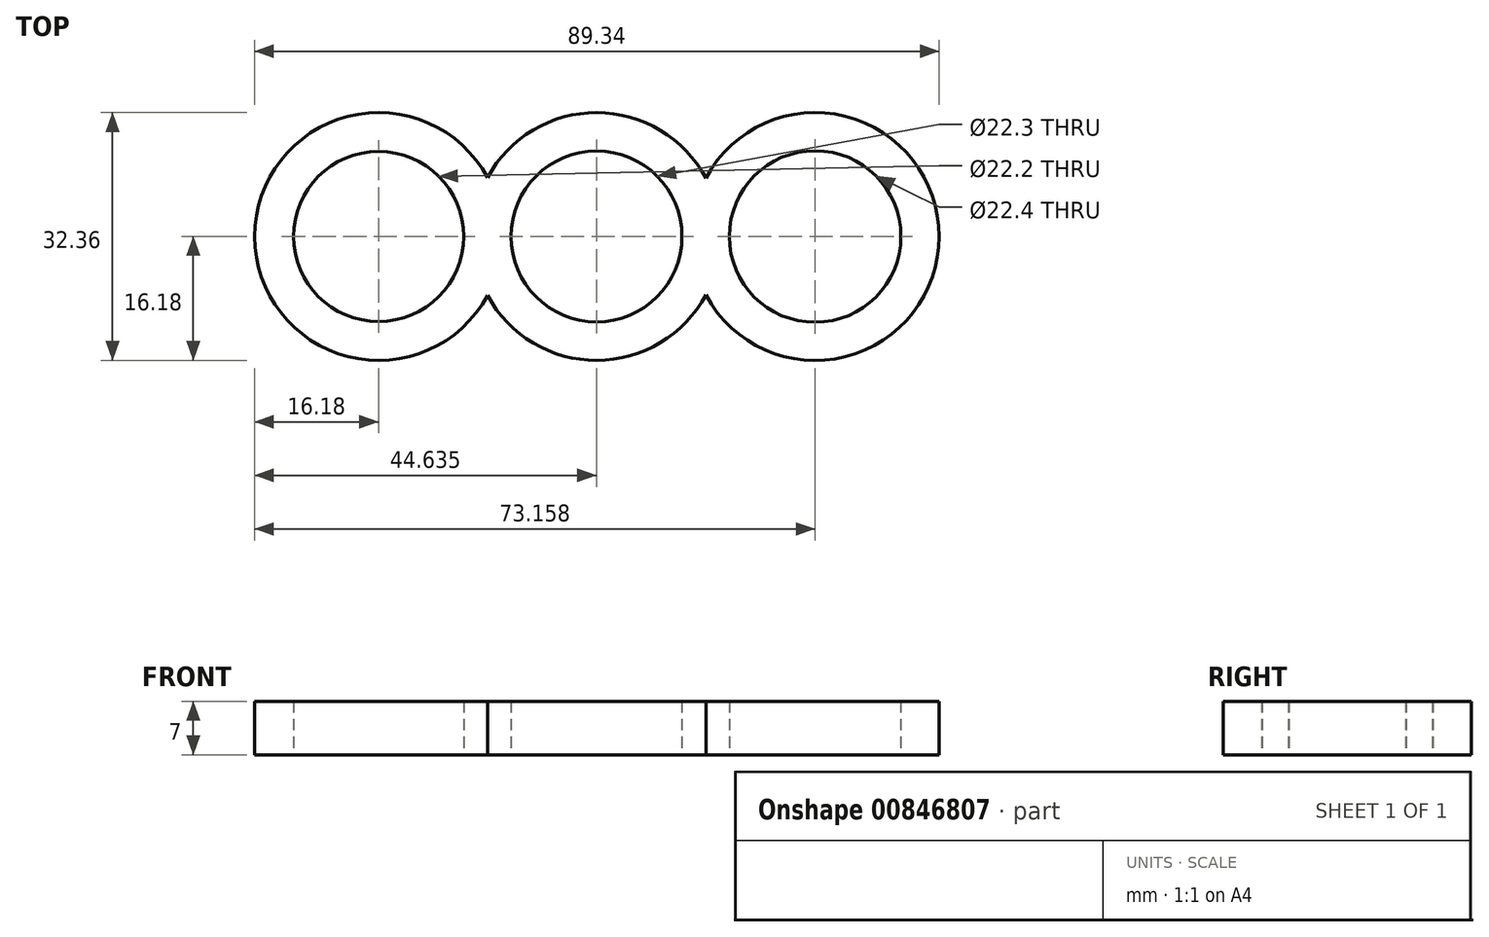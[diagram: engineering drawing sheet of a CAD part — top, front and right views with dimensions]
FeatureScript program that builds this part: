
annotation { "Feature Type Name" : "Feature", "Feature Type Description" : "" }
export const myFeature = defineFeature(function(context is Context, id is Id, definition is map)
    precondition{}
    {
        {
            var Q0;
            Q0=qCreatedBy(makeId("Top.planeOp"),FACE);
            var sketch = newSketch(context, id + "F0", { "sketchPlane" : qUnion([Q0])});
            skCircle(sketch, "E0", {"center": v(-43.1, 0) * mm, "radius": 16.18 * mm});
            skCircle(sketch, "E1", {"center": v(-43.1, 0) * mm, "radius": 11.05 * mm});
            skLineSegment(sketch, "E2", {"start": v(0, 0) * mm, "end": v(-76.05, 0) * mm});
            skLineSegment(sketch, "E3", {"start": v(0, 0) * mm, "end": v(76.92, 0) * mm});
            skCircle(sketch, "E4", {"center": v(-15.2, 0) * mm, "radius": 16.18 * mm});
            skCircle(sketch, "E5", {"center": v(-15.2, 0) * mm, "radius": 11.1 * mm});
            skCircle(sketch, "E6", {"center": v(13.25, 0) * mm, "radius": 16.18 * mm});
            skCircle(sketch, "E7", {"center": v(13.25, 0) * mm, "radius": 11.15 * mm});
            skCircle(sketch, "E8", {"center": v(41.78, 0) * mm, "radius": 16.18 * mm});
            skCircle(sketch, "E9", {"center": v(41.78, 0) * mm, "radius": 11.2 * mm});
            skSolve(sketch);
        }
        {
            var Q0;
            {var subQ0=sQuery(id+"F0.wireOp",EDGE,"E2");var subQ1=sQuery(id+"F0.wireOp",EDGE,"E0");var subQ2=makeQuery(id+"F0.imprint","INTERSECT",VERTEX,{"disambiguationData":[OD(0.0)],"derivedFrom":[subQ1,subQ0]});Q0=makeQuery(id+"F0.imprint","IMPRINT",FACE,{"disambiguationData":[TD([[makeQuery(id+"F0.imprint","IMPRINT",EDGE,{"disambiguationData":[TD([[subQ2,1.0]])],"derivedFrom":subQ1}),1.0]])]});}
            var Q1;
            {var subQ0=sQuery(id+"F0.wireOp",EDGE,"E2");var subQ1=sQuery(id+"F0.wireOp",EDGE,"E0");var subQ2=makeQuery(id+"F0.imprint","INTERSECT",VERTEX,{"disambiguationData":[OD(0.0)],"derivedFrom":[subQ1,subQ0]});Q1=makeQuery(id+"F0.imprint","IMPRINT",FACE,{"disambiguationData":[TD([[makeQuery(id+"F0.imprint","IMPRINT",EDGE,{"disambiguationData":[TD([[subQ2,-1.0]])],"derivedFrom":subQ1}),1.0]])]});}
            var Q2;
            {var subQ0=sQuery(id+"F0.wireOp",EDGE,"E4");var subQ1=sQuery(id+"F0.wireOp",EDGE,"E0");var subQ2=makeQuery(id+"F0.imprint","INTERSECT",VERTEX,{"disambiguationData":[OD(1.0)],"derivedFrom":[subQ1,subQ0]});Q2=makeQuery(id+"F0.imprint","IMPRINT",FACE,{"disambiguationData":[TD([[makeQuery(id+"F0.imprint","IMPRINT",EDGE,{"disambiguationData":[TD([[subQ2,-1.0]])],"derivedFrom":subQ1}),1.0]])]});}
            var Q3;
            {var subQ0=sQuery(id+"F0.wireOp",EDGE,"E4");var subQ1=sQuery(id+"F0.wireOp",EDGE,"E0");var subQ2=makeQuery(id+"F0.imprint","INTERSECT",VERTEX,{"disambiguationData":[OD(0.0)],"derivedFrom":[subQ1,subQ0]});Q3=makeQuery(id+"F0.imprint","IMPRINT",FACE,{"disambiguationData":[TD([[makeQuery(id+"F0.imprint","IMPRINT",EDGE,{"disambiguationData":[TD([[subQ2,1.0]])],"derivedFrom":subQ1}),1.0]])]});}
            var Q4;
            {var subQ0=sQuery(id+"F0.wireOp",EDGE,"E4");var subQ1=sQuery(id+"F0.wireOp",EDGE,"E0");var subQ2=makeQuery(id+"F0.imprint","INTERSECT",VERTEX,{"disambiguationData":[OD(0.0)],"derivedFrom":[subQ1,subQ0]});Q4=makeQuery(id+"F0.imprint","IMPRINT",FACE,{"disambiguationData":[TD([[makeQuery(id+"F0.imprint","IMPRINT",EDGE,{"disambiguationData":[TD([[subQ2,1.0]])],"derivedFrom":subQ1}),-1.0]])]});}
            var Q5;
            {var subQ0=sQuery(id+"F0.wireOp",EDGE,"E4");var subQ1=sQuery(id+"F0.wireOp",EDGE,"E0");var subQ2=makeQuery(id+"F0.imprint","INTERSECT",VERTEX,{"disambiguationData":[OD(1.0)],"derivedFrom":[subQ1,subQ0]});Q5=makeQuery(id+"F0.imprint","IMPRINT",FACE,{"disambiguationData":[TD([[makeQuery(id+"F0.imprint","IMPRINT",EDGE,{"disambiguationData":[TD([[subQ2,-1.0]])],"derivedFrom":subQ1}),-1.0]])]});}
            var Q6;
            {var subQ0=sQuery(id+"F0.wireOp",EDGE,"E3");var subQ1=sQuery(id+"F0.wireOp",EDGE,"E2");var subQ2=makeQuery(id+"F0.imprint","INTERSECT",VERTEX,{"derivedFrom":[subQ1,subQ0]});Q6=makeQuery(id+"F0.imprint","IMPRINT",FACE,{"disambiguationData":[TD([[makeQuery(id+"F0.imprint","IMPRINT",EDGE,{"disambiguationData":[TD([[subQ2,-1.0]])],"derivedFrom":subQ1}),1.0]])]});}
            var Q7;
            {var subQ0=sQuery(id+"F0.wireOp",EDGE,"E3");var subQ1=sQuery(id+"F0.wireOp",EDGE,"E2");var subQ2=makeQuery(id+"F0.imprint","INTERSECT",VERTEX,{"derivedFrom":[subQ1,subQ0]});Q7=makeQuery(id+"F0.imprint","IMPRINT",FACE,{"disambiguationData":[TD([[makeQuery(id+"F0.imprint","IMPRINT",EDGE,{"disambiguationData":[TD([[subQ2,-1.0]])],"derivedFrom":subQ1}),-1.0]])]});}
            var Q8;
            {var subQ1=sQuery(id+"F0.wireOp",EDGE,"E4");var subQ5=sQuery(id+"F0.wireOp",EDGE,"E3");var subQ6=makeQuery(id+"F0.imprint","INTERSECT",VERTEX,{"derivedFrom":[subQ5,subQ1]});Q8=makeQuery(id+"F0.imprint","IMPRINT",FACE,{"disambiguationData":[TD([[makeQuery(id+"F0.imprint","IMPRINT",EDGE,{"disambiguationData":[TD([[subQ6,-1.0]])],"derivedFrom":subQ5}),1.0]])]});}
            var Q9;
            {var subQ1=sQuery(id+"F0.wireOp",EDGE,"E4");var subQ5=sQuery(id+"F0.wireOp",EDGE,"E3");var subQ6=makeQuery(id+"F0.imprint","INTERSECT",VERTEX,{"derivedFrom":[subQ5,subQ1]});Q9=makeQuery(id+"F0.imprint","IMPRINT",FACE,{"disambiguationData":[TD([[makeQuery(id+"F0.imprint","IMPRINT",EDGE,{"disambiguationData":[TD([[subQ6,-1.0]])],"derivedFrom":subQ5}),-1.0]])]});}
            var Q10;
            {var subQ0=sQuery(id+"F0.wireOp",EDGE,"E8");var subQ1=sQuery(id+"F0.wireOp",EDGE,"E3");var subQ2=makeQuery(id+"F0.imprint","INTERSECT",VERTEX,{"disambiguationData":[OD(1.0)],"derivedFrom":[subQ1,subQ0]});Q10=makeQuery(id+"F0.imprint","IMPRINT",FACE,{"disambiguationData":[TD([[makeQuery(id+"F0.imprint","IMPRINT",EDGE,{"disambiguationData":[TD([[subQ2,-1.0]])],"derivedFrom":subQ1}),-1.0]])]});}
            var Q11;
            {var subQ0=sQuery(id+"F0.wireOp",EDGE,"E8");var subQ1=sQuery(id+"F0.wireOp",EDGE,"E3");var subQ2=makeQuery(id+"F0.imprint","INTERSECT",VERTEX,{"disambiguationData":[OD(1.0)],"derivedFrom":[subQ1,subQ0]});Q11=makeQuery(id+"F0.imprint","IMPRINT",FACE,{"disambiguationData":[TD([[makeQuery(id+"F0.imprint","IMPRINT",EDGE,{"disambiguationData":[TD([[subQ2,-1.0]])],"derivedFrom":subQ1}),1.0]])]});}
            var Q12;
            {var subQ1=sQuery(id+"F0.wireOp",EDGE,"E3");var subQ3=sQuery(id+"F0.wireOp",EDGE,"E6");var subQ5=makeQuery(id+"F0.imprint","INTERSECT",VERTEX,{"derivedFrom":[subQ1,subQ3]});Q12=makeQuery(id+"F0.imprint","IMPRINT",FACE,{"disambiguationData":[TD([[makeQuery(id+"F0.imprint","IMPRINT",EDGE,{"disambiguationData":[TD([[subQ5,-1.0]])],"derivedFrom":subQ1}),1.0]])]});}
            var Q13;
            {var subQ1=sQuery(id+"F0.wireOp",EDGE,"E6");var subQ3=sQuery(id+"F0.wireOp",EDGE,"E3");var subQ4=makeQuery(id+"F0.imprint","INTERSECT",VERTEX,{"derivedFrom":[subQ3,subQ1]});Q13=makeQuery(id+"F0.imprint","IMPRINT",FACE,{"disambiguationData":[TD([[makeQuery(id+"F0.imprint","IMPRINT",EDGE,{"disambiguationData":[TD([[subQ4,-1.0]])],"derivedFrom":subQ3}),-1.0]])]});}
            extrude(context, id + "F1", {"entities" : qUnion([Q0, Q1, Q2, Q3, Q4, Q5, Q6, Q7, Q8, Q9, Q10, Q11, Q12, Q13]), "depth" : 7 * mm, "offsetDistance" : 25.4 * mm});
        }
    });
